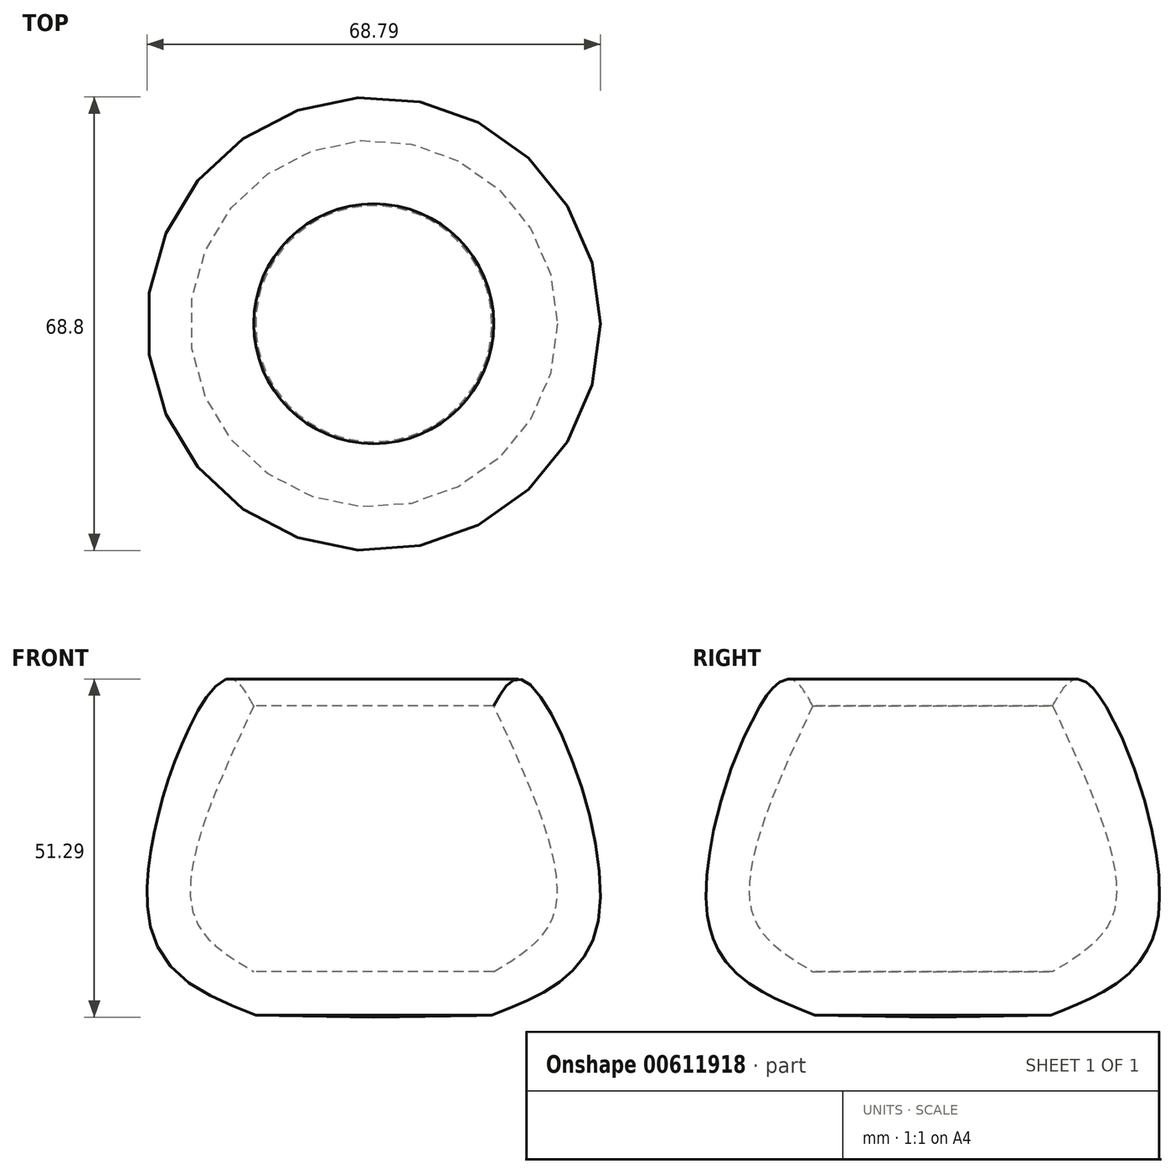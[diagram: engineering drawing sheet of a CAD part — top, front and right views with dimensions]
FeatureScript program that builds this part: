
annotation { "Feature Type Name" : "Feature", "Feature Type Description" : "" }
export const myFeature = defineFeature(function(context is Context, id is Id, definition is map)
    precondition{}
    {
        {
            var Q0;
            Q0=qCreatedBy(makeId("Front.planeOp"),FACE);
            var sketch = newSketch(context, id + "F0", { "sketchPlane" : qUnion([Q0])});
            skLineSegment(sketch, "E0", {"start": v(0, 52.19) * mm, "end": v(0, 0) * mm, "construction": true});
            skLineSegment(sketch, "E1", {"start": v(0, 10.38) * mm, "end": v(-17.9, 10.68) * mm});
            skLineSegment(sketch, "E2", {"start": v(0, 17.3) * mm, "end": v(-18.2, 17.3) * mm});
            skFitSpline(sketch, "E3", {"points": [v(-18.2, 17.3) * mm, v(-27.52, 26.62) * mm, v(-18.2, 57.6) * mm], "startDerivative": vector(-31.57, 18.7) * mm, "endDerivative": vector(27.24, 58.95) * mm});
            skFitSpline(sketch, "E4", {"points": [v(-18.2, 57.6) * mm, v(-22.7, 61.51) * mm, v(-34.14, 25.42) * mm, v(-17.9, 10.68) * mm], "startDerivative": vector(-21.32, 38.56) * mm, "endDerivative": vector(63.08, -24.57) * mm});
            skLineSegment(sketch, "E5", {"start": v(0, 17.3) * mm, "end": v(0, 10.38) * mm});
            skSolve(sketch);
        }
        {
            var Q0;
            Q0=makeQuery(id+"F0.imprint","IMPRINT",FACE,{"disambiguationData":[TD([[makeQuery(id+"F0.imprint","IMPRINT",EDGE,{"derivedFrom":sQuery(id+"F0.wireOp",EDGE,"E1")}),-1.0]])]});
            var Q1;
            Q1=sQuery(id+"F0.wireOp",EDGE,"E0");
            revolve(context, id + "F1", {"entities" : qUnion([Q0]), "axis" : qUnion([Q1]), "revolveType" : RevolveType.FULL});
        }
    });
